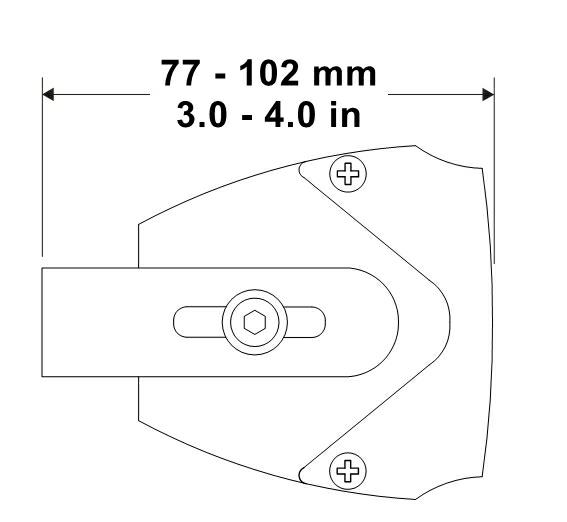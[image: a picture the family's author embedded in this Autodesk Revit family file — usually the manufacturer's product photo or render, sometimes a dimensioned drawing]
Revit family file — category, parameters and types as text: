
# Revit family: Electronics_Desono_Biamp_Two-Way-Column-Loudspeaker_COLS81
name_source: partatom
category: Communication Devices
units: mm (PartAtom-declared; Revit-internal decimal feet)

## family parameters
Cut with Voids When Loaded = No
Host = Face
Maintain Annotation Orientation = No
OmniClass Number = 23.85.10.11.14.14.14
OmniClass Title = Loudspeakers
Part Type = Normal
Room Calculation Point = No
Round Connector Dimension = Use Diameter
Shared = No

## types (1)
- COLS81
    Bracket Material = Biamp - Metal - White
    Connector Description = Terminal block; Low impedance 16 ohms; 70V/100V operation
    Continuous Power Handling Nominal Impedance = 22V; 30W @ 16Ω (120W peak)
    Controls = None; select transformer tap or low impedance input via terminal block wiring
    Default Elevation = 4' - 0"
    Depth = 0' - 2 1/2"
    Description = Desono™ COLS81 Two-Way 8 x 2 Column Loudspeaker
    Environmental = IP66 per IEC 60529
    Grill Material = Biamp - Plastic - White(Grid)
    Height = 2' - 0"
    Housing Material = Biamp - Plastic - White
    Input Connection = Multi-position pass-through, screw-down terminal block
    Manufacturer = Biamp
    Model = COLS81
    Mounting Provisions = Adjustable tilt L-bracket
    Nominal Beamwidth (H x V) = 120° x 15°
    Nominal Maximum SPL @ 1m = Peak - 110dB; Continuous - 104dB
    Nominal Sensitivity @ 1m = 1W - 89dB; 2.83V - 86dB
    Operating Environment = Indoor/Outdoor
    Operating Mode = Passive
    Operating Range 2 (-10dB) = 185 Hz to 22 kHz
    Product Documentation Link = https://downloads.biamp.com
    Product Page URL = https://www.biamp.com
    Product data url = https://www.bimobject.com
    Recommended Amplifers = 30W - 60W @ 16Ω (22V - 31V)
    Shipping Weight = 7.30 lb
    Transducers = LF 8 x 2 (51 mm) coated paper cone HF 1 x 1 (25 mm) soft dome
    Transformer = 70V: 30W, 15W, 7.5W, 3W; 100V: 30W, 15W, 7.5W
    URL = https://www.biamp.com
    Weight = 6.40 lb
    Width = 0' - 2 1/2"

## geometry (parser evidence)
native form markers: Sweep x5
no freeform markers — native parametric forms only
